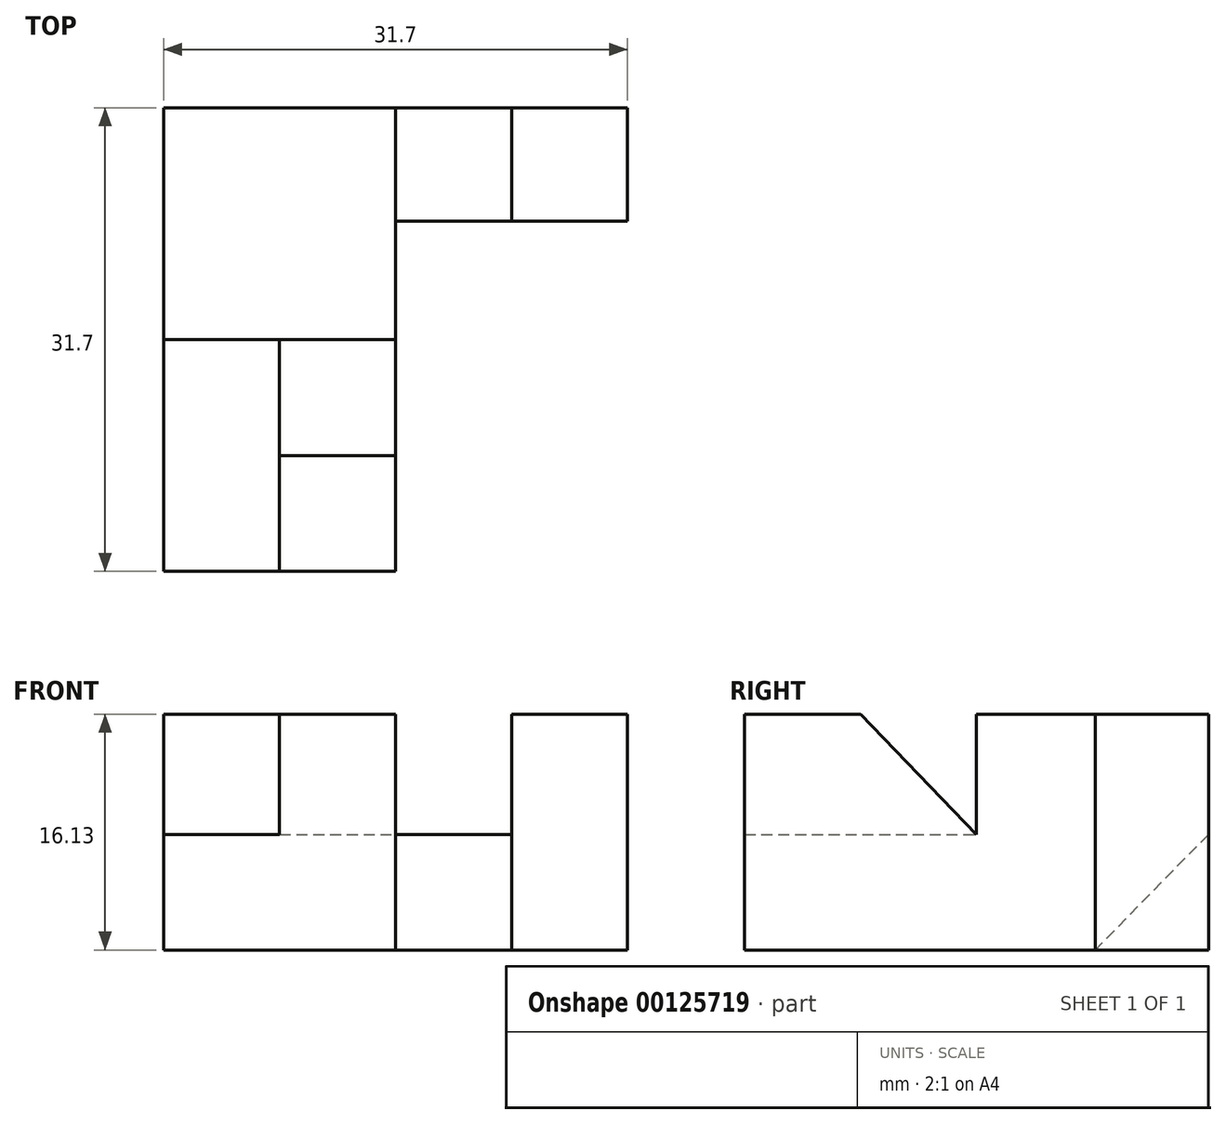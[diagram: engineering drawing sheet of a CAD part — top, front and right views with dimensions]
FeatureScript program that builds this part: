
annotation { "Feature Type Name" : "Feature", "Feature Type Description" : "" }
export const myFeature = defineFeature(function(context is Context, id is Id, definition is map)
    precondition{}
    {
        {
            var Q0;
            Q0=qCreatedBy(makeId("Top.planeOp"),FACE);
            var sketch = newSketch(context, id + "F0", { "sketchPlane" : qUnion([Q0])});
            skLineSegment(sketch, "E0", {"start": v(0, 0) * mm, "end": v(31.7, 0) * mm});
            skLineSegment(sketch, "E1", {"start": v(31.7, 0) * mm, "end": v(31.7, 31.7) * mm});
            skLineSegment(sketch, "E2", {"start": v(31.7, 31.7) * mm, "end": v(0, 31.7) * mm});
            skLineSegment(sketch, "E3", {"start": v(0, 31.7) * mm, "end": v(0, 0) * mm});
            skSolve(sketch);
        }
        {
            var Q0;
            Q0=makeQuery(id+"F0.imprint","IMPRINT",FACE,{"disambiguationData":[TD([[makeQuery(id+"F0.imprint","IMPRINT",EDGE,{"derivedFrom":sQuery(id+"F0.wireOp",EDGE,"E0")}),1.0]])]});
            extrude(context, id + "F1", {"entities" : qUnion([Q0]), "depth" : 7.9 * mm});
        }
        {
            var Q0;
            Q0=makeQuery(id+"F1.opExtrude","CAP_FACE",FACE,{"disambiguationData":[OSD([sQuery(id+"F0.wireOp",EDGE,"E0"),sQuery(id+"F0.wireOp",EDGE,"E1"),sQuery(id+"F0.wireOp",EDGE,"E2"),sQuery(id+"F0.wireOp",EDGE,"E3")])],"isStart":false});
            var sketch = newSketch(context, id + "F2", { "sketchPlane" : qUnion([Q0])});
            skLineSegment(sketch, "E4", {"start": v(31.7, 0) * mm, "end": v(31.7, 23.95) * mm});
            skLineSegment(sketch, "E5", {"start": v(15.85, 23.95) * mm, "end": v(15.85, 0) * mm});
            skLineSegment(sketch, "E6", {"start": v(15.85, 0) * mm, "end": v(31.7, 0) * mm});
            skLineSegment(sketch, "E7", {"start": v(31.7, 23.95) * mm, "end": v(15.85, 23.95) * mm});
            skLineSegment(sketch, "E8", {"start": v(23.78, 23.95) * mm, "end": v(23.78, 31.7) * mm});
            skLineSegment(sketch, "E9", {"start": v(23.78, 31.7) * mm, "end": v(31.7, 31.7) * mm});
            skLineSegment(sketch, "E10", {"start": v(31.7, 31.7) * mm, "end": v(31.7, 23.95) * mm});
            skLineSegment(sketch, "E11", {"start": v(23.78, 23.95) * mm, "end": v(31.7, 23.95) * mm});
            skSolve(sketch);
        }
        {
            var Q0;
            Q0=makeQuery(id+"F2.imprint","IMPRINT",FACE,{"disambiguationData":[TD([[makeQuery(id+"F2.imprint","IMPRINT",EDGE,{"derivedFrom":sQuery(id+"F2.wireOp",EDGE,"E4")}),1.0]])]});
            extrude(context, id + "F3", {"entities" : qUnion([Q0]), "operationType" : NewBodyOperationType.REMOVE, "endBound" : BoundingType.THROUGH_ALL, "oppositeDirection" : true, "depth" : 25 * mm});
        }
        {
            var Q0;
            Q0=makeQuery(id+"F1.opExtrude","CAP_FACE",FACE,{"disambiguationData":[OSD([sQuery(id+"F0.wireOp",EDGE,"E0"),sQuery(id+"F0.wireOp",EDGE,"E1"),sQuery(id+"F0.wireOp",EDGE,"E2"),sQuery(id+"F0.wireOp",EDGE,"E3")])],"isStart":false});
            var sketch = newSketch(context, id + "F4", { "sketchPlane" : qUnion([Q0])});
            skLineSegment(sketch, "E12.0.0", {"start": v(23.78, 31.7) * mm, "end": v(23.78, 23.95) * mm});
            skLineSegment(sketch, "E12.0.1", {"start": v(23.78, 23.95) * mm, "end": v(31.7, 23.95) * mm});
            skLineSegment(sketch, "E12.0.2", {"start": v(31.7, 23.95) * mm, "end": v(31.7, 31.7) * mm});
            skLineSegment(sketch, "E12.0.3", {"start": v(31.7, 31.7) * mm, "end": v(23.78, 31.7) * mm});
            skSolve(sketch);
        }
        {
            var Q0;
            Q0 = qSketchRegion(id + "F4", true);
            var Q1;
            Q1=makeQuery(id+"F2.imprint","IMPRINT",FACE,{"disambiguationData":[TD([[makeQuery(id+"F2.imprint","IMPRINT",EDGE,{"derivedFrom":sQuery(id+"F2.wireOp",EDGE,"E8")}),-1.0]])]});
            extrude(context, id + "F5", {"entities" : qUnion([Q0, Q1]), "operationType" : NewBodyOperationType.ADD, "depth" : 8.23 * mm});
        }
        {
            var Q0;
            {var subQ3=sQuery(id+"F2.wireOp",EDGE,"E5");Q0=makeQuery(id+"F2.imprint","IMPRINT",FACE,{"disambiguationData":[TD([[makeQuery(id+"F2.imprint","IMPRINT",EDGE,{"derivedFrom":subQ3}),-1.0]])]});}
            extrude(context, id + "F6", {"entities" : qUnion([Q0]), "operationType" : NewBodyOperationType.ADD, "depth" : 8.23 * mm});
        }
        {
            var Q0;
            {var subQ0=sQuery(id+"F2.wireOp",EDGE,"E8");Q0=makeQuery(id+"F6.boolean.opBoolean","MERGE",FACE,{"derivedFrom":[makeQuery(id+"F5.opExtrude","CAP_FACE",FACE,{"disambiguationData":[OSD([subQ0,sQuery(id+"F2.wireOp",EDGE,"E9"),sQuery(id+"F2.wireOp",EDGE,"E10"),sQuery(id+"F2.wireOp",EDGE,"E11")])],"isStart":false}),makeQuery(id+"F6.opExtrude","CAP_FACE",FACE,{"disambiguationData":[OSD([sQuery(id+"F0.wireOp",EDGE,"E0"),sQuery(id+"F0.wireOp",EDGE,"E2"),sQuery(id+"F0.wireOp",EDGE,"E3"),sQuery(id+"F2.wireOp",EDGE,"E5"),sQuery(id+"F2.wireOp",EDGE,"E7"),subQ0])],"isStart":false})]});}
            var sketch = newSketch(context, id + "F7", { "sketchPlane" : qUnion([Q0])});
            skLineSegment(sketch, "E13", {"start": v(7.93, 0) * mm, "end": v(7.93, 7.92) * mm});
            skLineSegment(sketch, "E14", {"start": v(7.93, 7.92) * mm, "end": v(15.85, 7.92) * mm});
            skLineSegment(sketch, "E15", {"start": v(15.85, 7.92) * mm, "end": v(15.85, 0) * mm});
            skLineSegment(sketch, "E16", {"start": v(15.85, 0) * mm, "end": v(7.93, 0) * mm});
            skLineSegment(sketch, "E17", {"start": v(15.85, 31.7) * mm, "end": v(0, 31.7) * mm});
            skLineSegment(sketch, "E18", {"start": v(0, 31.7) * mm, "end": v(0, 15.85) * mm});
            skLineSegment(sketch, "E19", {"start": v(0, 15.85) * mm, "end": v(15.85, 15.85) * mm});
            skLineSegment(sketch, "E20", {"start": v(15.85, 15.85) * mm, "end": v(15.85, 31.7) * mm});
            skLineSegment(sketch, "E21", {"start": v(31.7, 31.7) * mm, "end": v(31.7, 23.95) * mm});
            skLineSegment(sketch, "E22", {"start": v(31.7, 23.95) * mm, "end": v(23.78, 23.95) * mm});
            skLineSegment(sketch, "E23", {"start": v(23.78, 23.95) * mm, "end": v(23.78, 31.7) * mm});
            skLineSegment(sketch, "E24", {"start": v(23.78, 31.7) * mm, "end": v(31.7, 31.7) * mm});
            skSolve(sketch);
        }
        {
            var Q0;
            {var subQ5=sQuery(id+"F7.wireOp",EDGE,"E23");Q0=makeQuery(id+"F7.imprint","IMPRINT",FACE,{"disambiguationData":[TD([[makeQuery(id+"F7.imprint","IMPRINT",EDGE,{"derivedFrom":subQ5}),1.0]])]});}
            var Q1;
            {var subQ3=sQuery(id+"F7.wireOp",EDGE,"E13");Q1=makeQuery(id+"F7.imprint","IMPRINT",FACE,{"disambiguationData":[TD([[makeQuery(id+"F7.imprint","IMPRINT",EDGE,{"derivedFrom":subQ3}),1.0]])]});}
            extrude(context, id + "F8", {"entities" : qUnion([Q0, Q1]), "operationType" : NewBodyOperationType.REMOVE, "oppositeDirection" : true, "depth" : 8.23 * mm});
        }
        {
            var Q0;
            {var subQ0=sQuery(id+"F2.wireOp",EDGE,"E5");Q0=makeQuery(id+"F8.boolean.opBoolean","MERGE",FACE,{"derivedFrom":[makeQuery(id+"F6.boolean.opBoolean","MERGE",FACE,{"derivedFrom":[makeQuery(id+"F3.boolean.opBoolean","COPY",FACE,{"derivedFrom":makeQuery(id+"F3.opExtrude","SWEPT_FACE",FACE,{"disambiguationData":[OSD([subQ0])]})}),makeQuery(id+"F6.opExtrude","SWEPT_FACE",FACE,{"disambiguationData":[OSD([subQ0])]})]}),makeQuery(id+"F8.opExtrude","SWEPT_FACE",FACE,{"disambiguationData":[OSD([sQuery(id+"F7.wireOp",EDGE,"E20")])]})]});}
            var sketch = newSketch(context, id + "F9", { "sketchPlane" : qUnion([Q0])});
            skLineSegment(sketch, "E25", {"start": v(7.92, 16.13) * mm, "end": v(15.85, 7.9) * mm});
            skLineSegment(sketch, "E26.0", {"start": v(0, 16.13) * mm, "end": v(7.92, 16.13) * mm});
            skLineSegment(sketch, "E27.0", {"start": v(7.92, 7.9) * mm, "end": v(7.92, 16.13) * mm});
            skLineSegment(sketch, "E28", {"start": v(7.92, 7.9) * mm, "end": v(15.85, 7.9) * mm});
            skSolve(sketch);
        }
        {
            var Q0;
            Q0=makeQuery(id+"F9.imprint","IMPRINT",FACE,{"disambiguationData":[TD([[makeQuery(id+"F9.imprint","IMPRINT",EDGE,{"derivedFrom":sQuery(id+"F9.wireOp",EDGE,"E25")}),-1.0]])]});
            var Q1;
            Q1=makeQuery(id+"F8.boolean.opBoolean","COPY",FACE,{"derivedFrom":makeQuery(id+"F8.opExtrude","SWEPT_FACE",FACE,{"disambiguationData":[OSD([sQuery(id+"F7.wireOp",EDGE,"E13")])]})});
            extrude(context, id + "F10", {"entities" : qUnion([Q0]), "operationType" : NewBodyOperationType.ADD, "endBound" : BoundingType.UP_TO_SURFACE, "oppositeDirection" : true, "endBoundEntityFace" : qUnion([Q1]), "depth" : 25 * mm});
        }
        {
            var Q0;
            {var subQ0=sQuery(id+"F2.wireOp",EDGE,"E5");Q0=makeQuery(id+"F10.boolean.opBoolean","MERGE",FACE,{"derivedFrom":[makeQuery(id+"F8.boolean.opBoolean","MERGE",FACE,{"derivedFrom":[makeQuery(id+"F6.boolean.opBoolean","MERGE",FACE,{"derivedFrom":[makeQuery(id+"F3.boolean.opBoolean","COPY",FACE,{"derivedFrom":makeQuery(id+"F3.opExtrude","SWEPT_FACE",FACE,{"disambiguationData":[OSD([subQ0])]})}),makeQuery(id+"F6.opExtrude","SWEPT_FACE",FACE,{"disambiguationData":[OSD([subQ0])]})]}),makeQuery(id+"F8.opExtrude","SWEPT_FACE",FACE,{"disambiguationData":[OSD([sQuery(id+"F7.wireOp",EDGE,"E20")])]})]}),makeQuery(id+"F10.opExtrude","CAP_FACE",FACE,{"disambiguationData":[OSD([sQuery(id+"F9.wireOp",EDGE,"E25"),sQuery(id+"F9.wireOp",EDGE,"E27.0"),sQuery(id+"F9.wireOp",EDGE,"E28")])],"isStart":true})]});}
            var sketch = newSketch(context, id + "F11", { "sketchPlane" : qUnion([Q0])});
            skLineSegment(sketch, "E29", {"start": v(31.7, 7.9) * mm, "end": v(23.95, 0) * mm});
            skLineSegment(sketch, "E30", {"start": v(23.95, 0) * mm, "end": v(23.95, 7.9) * mm});
            skLineSegment(sketch, "E31", {"start": v(23.95, 7.9) * mm, "end": v(31.7, 7.9) * mm});
            skSolve(sketch);
        }
        {
            var Q0;
            Q0 = qSketchRegion(id + "F11", true);
            var Q1;
            Q1=makeQuery(id+"F8.boolean.opBoolean","COPY",FACE,{"derivedFrom":makeQuery(id+"F8.opExtrude","SWEPT_FACE",FACE,{"disambiguationData":[OSD([sQuery(id+"F7.wireOp",EDGE,"E23")])]})});
            extrude(context, id + "F12", {"entities" : qUnion([Q0]), "operationType" : NewBodyOperationType.REMOVE, "endBound" : BoundingType.UP_TO_SURFACE, "endBoundEntityFace" : qUnion([Q1]), "depth" : 25 * mm});
        }
    });
